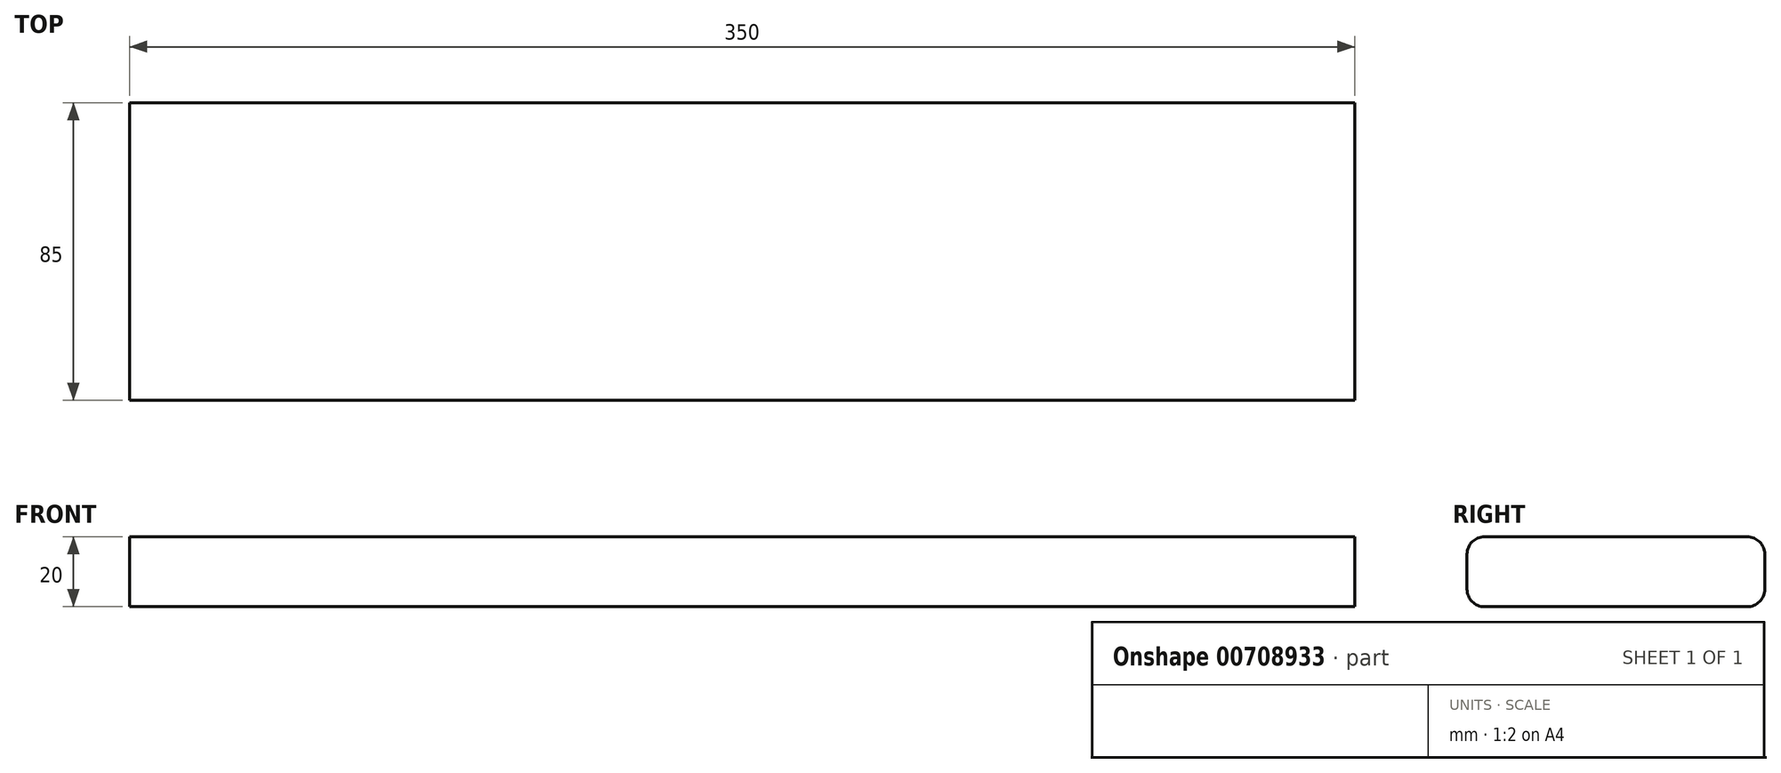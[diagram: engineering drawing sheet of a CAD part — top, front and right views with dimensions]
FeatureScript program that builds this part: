
annotation { "Feature Type Name" : "Feature", "Feature Type Description" : "" }
export const myFeature = defineFeature(function(context is Context, id is Id, definition is map)
    precondition{}
    {
        {
            var Q0;
            Q0=qCreatedBy(makeId("Right.planeOp"),FACE);
            var sketch = newSketch(context, id + "F0", { "sketchPlane" : qUnion([Q0])});
            skLineSegment(sketch, "E0.bottom", {"start": v(37.5, 10) * mm, "end": v(-37.5, 10) * mm});
            skLineSegment(sketch, "E0.top", {"start": v(37.5, -10) * mm, "end": v(-37.5, -10) * mm});
            skLineSegment(sketch, "E0.left", {"start": v(42.5, 5) * mm, "end": v(42.5, -5) * mm});
            skLineSegment(sketch, "E0.right", {"start": v(-42.5, 5) * mm, "end": v(-42.5, -5) * mm});
            skPoint(sketch, "E0.middle", {"position": v(0, 0) * mm});
            skPoint(sketch, "E1.visualSharp", {"position": v(-42.5, 10) * mm});
            skArc(sketch, "E1.filletArc", {"start": v(-37.5, 10) * mm, "mid": v(-41.04, 8.54) * mm, "end": v(-42.5, 5) * mm});
            skPoint(sketch, "E2.visualSharp", {"position": v(-42.5, -10) * mm});
            skArc(sketch, "E2.filletArc", {"start": v(-42.5, -5) * mm, "mid": v(-41.04, -8.54) * mm, "end": v(-37.5, -10) * mm});
            skPoint(sketch, "E3.visualSharp", {"position": v(42.5, -10) * mm});
            skArc(sketch, "E3.filletArc", {"start": v(37.5, -10) * mm, "mid": v(41.04, -8.54) * mm, "end": v(42.5, -5) * mm});
            skPoint(sketch, "E4.visualSharp", {"position": v(42.5, 10) * mm});
            skArc(sketch, "E4.filletArc", {"start": v(42.5, 5) * mm, "mid": v(41.04, 8.54) * mm, "end": v(37.5, 10) * mm});
            skSolve(sketch);
        }
        {
            var Q0;
            Q0=makeQuery(id+"F0.imprint","IMPRINT",FACE,{"disambiguationData":[TD([[makeQuery(id+"F0.imprint","IMPRINT",EDGE,{"derivedFrom":sQuery(id+"F0.wireOp",EDGE,"E0.bottom")}),1.0]])]});
            extrude(context, id + "F1", {"entities" : qUnion([Q0]), "endBound" : BoundingType.SYMMETRIC, "depth" : 350 * mm, "offsetDistance" : 25 * mm});
        }
    });
